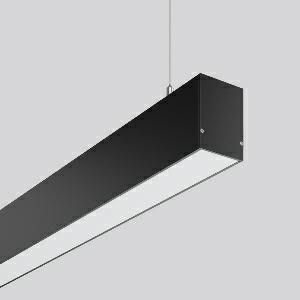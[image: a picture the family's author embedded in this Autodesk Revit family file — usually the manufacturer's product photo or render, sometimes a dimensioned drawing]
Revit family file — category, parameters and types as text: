
# Revit family: less_is_more_50_312317_003_1_76_97c2
name_source: partatom
category: Lighting Fixtures
units: mm (PartAtom-declared; Revit-internal decimal feet)

## family parameters
Cut with Voids When Loaded = No
Host = Face
Light Source = No
Part Type = Normal
Room Calculation Point = No
Round Connector Dimension = Use Diameter
Shared = No

## types (1)
- LESS IS MORE 50 (1 x LED Modul 840, 4000 lm, 4000)
    Apparent Load = 34 VA
    CIE Flux Codes = 49 80 96 63 100
    Color Rendering = 80
    Color Temperature = 4000
    Default Elevation = 1800 mm
    Description = Series: LESS IS MORE 50
Linear pendant luminaire for aesthetically sophisticated lighting. Housing: extruded aluminium profile, powder-coated. End cap aluminium powder-coated. Canopy made of aluminium, powder-coated. Diffuser made of non-yellowing plastic (PMMA), opal. Direct 65%, indirect 35% light emission. Suitable for pendant. 2-point steel cable suspension freely positionable and infinitely height-adjustable. Special lengths available on request. LED unit with integrated converter interchangeable and removable. Suitable for through-wiring. With sensors or as a safety luminaire on request. 
Colour: deep black, matt (RAL 9005)
Length: 847 mm
Width: 57 mm
Height: 75 mm
Suspension length: 2000 mm
Lamp: LED
Socket: without socket
Colour temperature: 4000K
Colour rendering index (CRI): 80
Light source: LED
Socket lamp2: Without base
Colour temperature: 4000K
System power: 34 W
Rated luminous flux: 4000 lm
Luminous efficiency: 118 lm/W
Control gear: Converter, dimmable, DALI
Control gear: Converter, dimmable, DALI
Protection class: I
Type of protection: IP 20
    Height = 75 mm
    Lamp = 1 x LED Modul 840
    Lamp Light Flux = 4000 lm
    Lamp count = 1
    Length = 847 mm
    Lifetime = 50000 h
    Luminous efficacy = 118 lm/W
    Manufacturer = RZB
    ModVariant = No
    Model = 312317.003.1.76
    Mounting Place = Ceiling
    Mounting Type = Pendant
    Number of Poles = 1
    OnlyDefault = Yes
    Power Factor = 1
    Product Name = LESS IS MORE 50
    Product group = Pendant LED linear luminaires
    ProductGroupID = 907
    Protection Class = Protection class I
    Protection Degree = IP 20
    RLX_Detail_Level = 1
    RLX_Emergency_Light_Flux = 0 lm
    RLX_Emergency_Type = 0
    RLX_Emergency_Type_DB = No
    RlxData = <blob elided: 39905 chars, md5=99f1a741>
    Socket = socket
    Standby Power = 0 W
    System Light Flux = 4000 lm
    System Power = 34 W
    Type Comments = Product without accessories
    Type Image = 312318.003.jpg
    URL = http://relux.com
    VarID = ---
    Voltage = 230 V
    Voltage Range = 220-240 V
    Weight = 0.00 kg
    Width = 57 mm

## geometry (parser evidence)
native form markers: Blend x4, Sweep x12
no freeform markers — native parametric forms only
